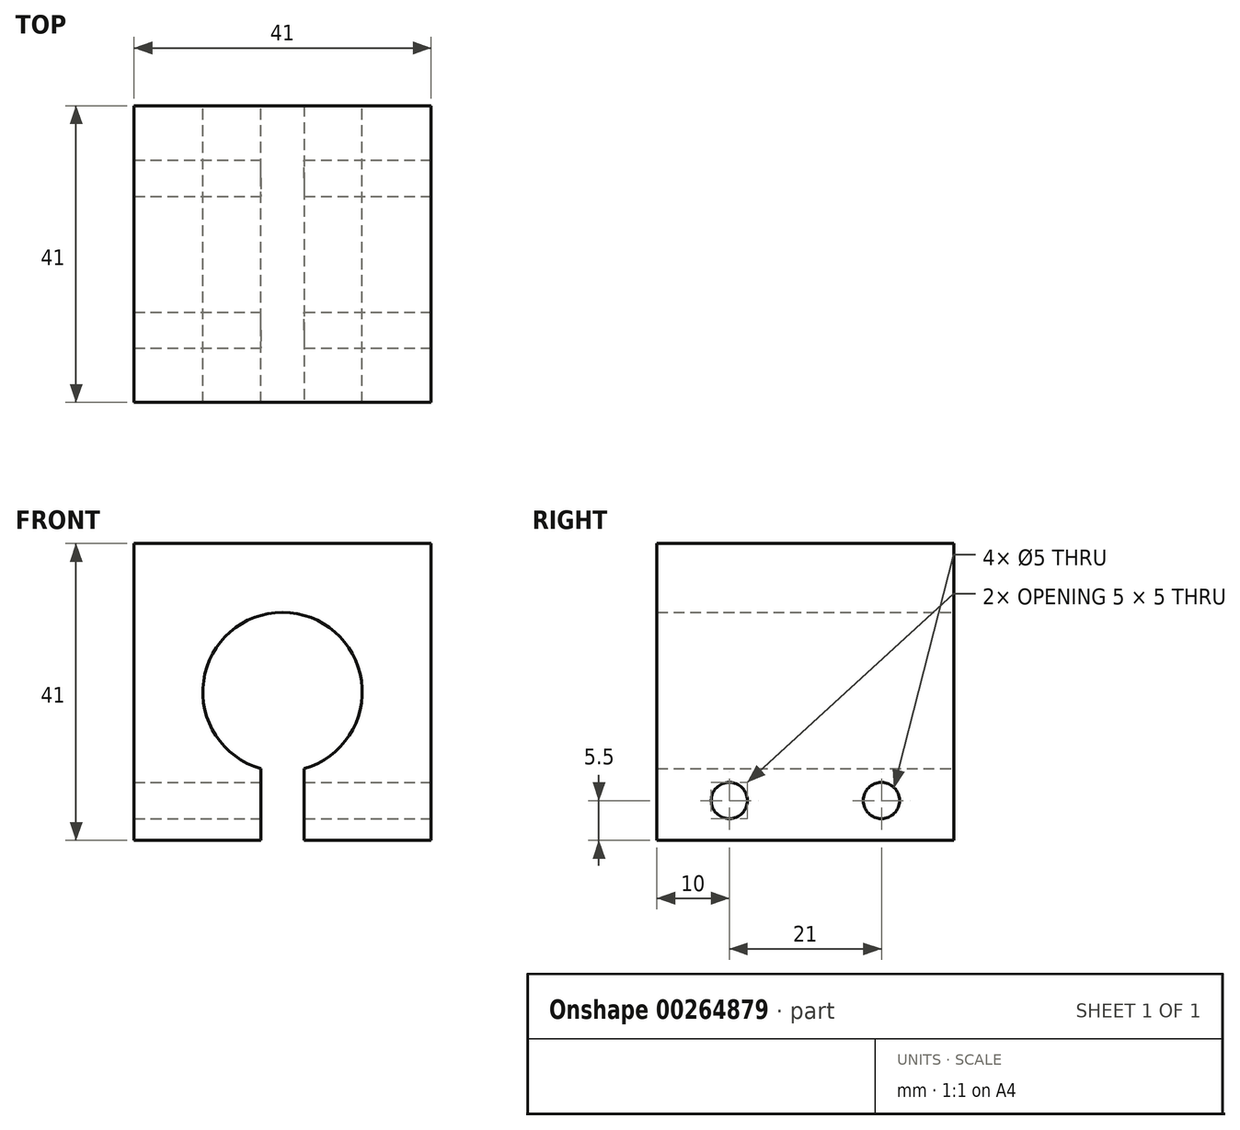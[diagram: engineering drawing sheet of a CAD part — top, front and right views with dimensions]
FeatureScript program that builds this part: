
annotation { "Feature Type Name" : "Feature", "Feature Type Description" : "" }
export const myFeature = defineFeature(function(context is Context, id is Id, definition is map)
    precondition{}
    {
        {
            var Q0;
            Q0=qCreatedBy(makeId("Front.planeOp"),FACE);
            var sketch = newSketch(context, id + "F0", { "sketchPlane" : qUnion([Q0])});
            skLineSegment(sketch, "E0.bottom", {"start": v(-20.5, 20.5) * mm, "end": v(20.5, 20.5) * mm});
            skLineSegment(sketch, "E0.top", {"start": v(-20.5, -20.5) * mm, "end": v(20.5, -20.5) * mm});
            skLineSegment(sketch, "E0.left", {"start": v(-20.5, 20.5) * mm, "end": v(-20.5, -20.5) * mm});
            skLineSegment(sketch, "E0.right", {"start": v(20.5, 20.5) * mm, "end": v(20.5, -20.5) * mm});
            skPoint(sketch, "E0.middle", {"position": v(0, 0) * mm});
            skCircle(sketch, "E1", {"center": v(0, 0) * mm, "radius": 11 * mm});
            skSolve(sketch);
        }
        {
            var Q0;
            Q0 = qSketchRegion(id + "F0", true);
            var Q1;
            Q1=makeQuery(id+"F0.imprint","IMPRINT",FACE,{"disambiguationData":[TD([[makeQuery(id+"F0.imprint","IMPRINT",EDGE,{"derivedFrom":sQuery(id+"F0.wireOp",EDGE,"wRl4ZfbD-Ujiz-kh3I-UFaE-ptS8EyVXeiUd.bottom")}),-1.0]])]});
            extrude(context, id + "F1", {"entities" : qUnion([Q0, Q1]), "depth" : 41 * mm});
        }
        {
            var Q0;
            Q0=qCreatedBy(makeId("Front.planeOp"),FACE);
            var sketch = newSketch(context, id + "F2", { "sketchPlane" : qUnion([Q0])});
            skLineSegment(sketch, "E2.bottom", {"start": v(3, -20.7) * mm, "end": v(-3, -20.7) * mm});
            skLineSegment(sketch, "E2.top", {"start": v(3, -9.2) * mm, "end": v(-3, -9.2) * mm});
            skLineSegment(sketch, "E2.left", {"start": v(3, -20.7) * mm, "end": v(3, -9.2) * mm});
            skLineSegment(sketch, "E2.right", {"start": v(-3, -20.7) * mm, "end": v(-3, -9.2) * mm});
            skPoint(sketch, "E2.middle", {"position": v(0, -14.96) * mm});
            skSolve(sketch);
        }
        {
            var Q0;
            Q0 = qSketchRegion(id + "F2", true);
            extrude(context, id + "F3", {"entities" : qUnion([Q0]), "operationType" : NewBodyOperationType.REMOVE, "endBound" : BoundingType.THROUGH_ALL, "depth" : 25.4 * mm});
        }
        {
            var Q0;
            Q0=makeQuery(id+"F1.opExtrude","SWEPT_FACE",FACE,{"disambiguationData":[OSD([sQuery(id+"F0.wireOp",EDGE,"E0.right")])]});
            var sketch = newSketch(context, id + "F4", { "sketchPlane" : qUnion([Q0])});
            skCircle(sketch, "E3", {"center": v(-31, -15) * mm, "radius": 2.5 * mm});
            skCircle(sketch, "E4", {"center": v(-10, -15) * mm, "radius": 2.5 * mm});
            skSolve(sketch);
        }
        {
            var Q0;
            Q0 = qSketchRegion(id + "F4", true);
            extrude(context, id + "F5", {"entities" : qUnion([Q0]), "operationType" : NewBodyOperationType.REMOVE, "endBound" : BoundingType.THROUGH_ALL, "oppositeDirection" : true, "depth" : 25.4 * mm});
        }
    });
